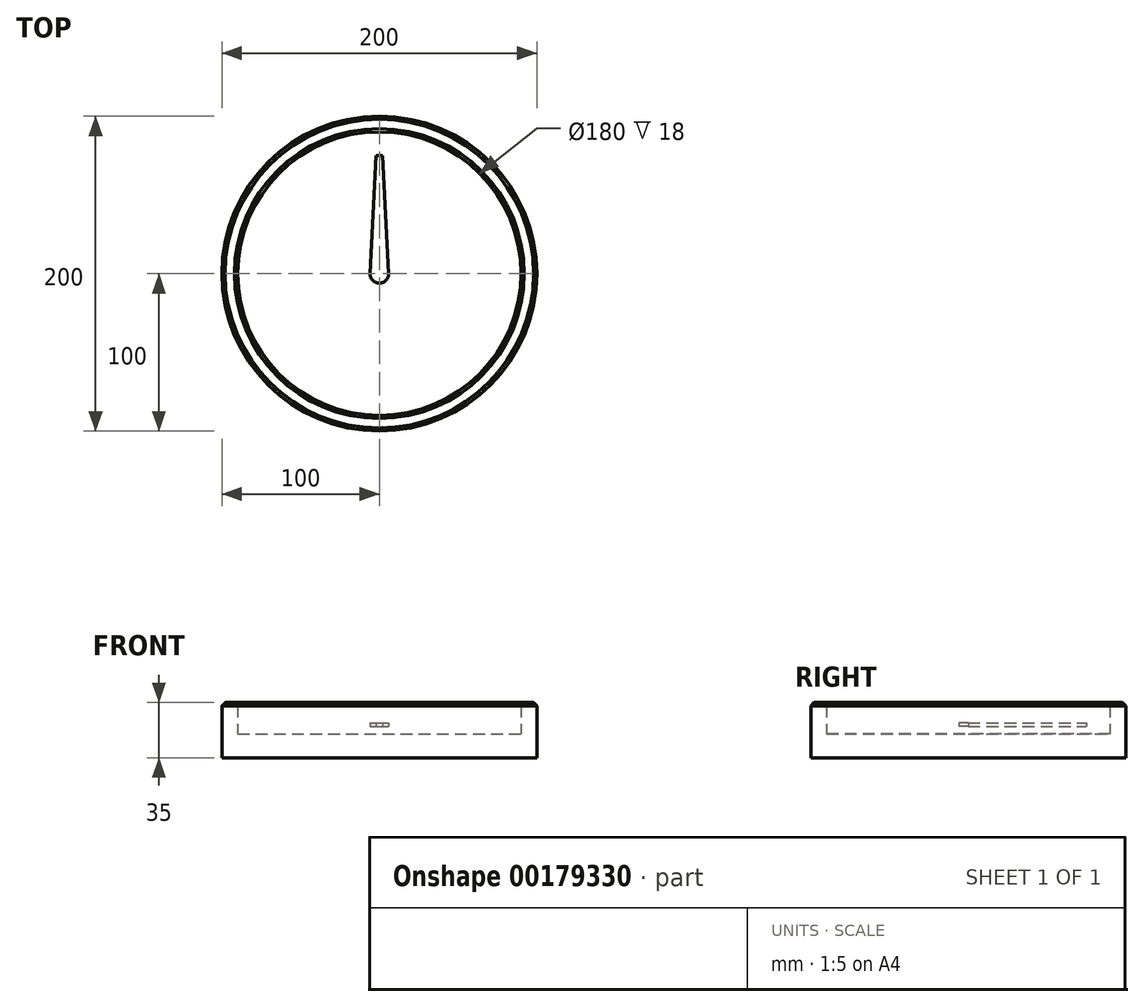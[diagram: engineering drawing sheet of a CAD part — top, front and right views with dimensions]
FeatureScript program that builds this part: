
annotation { "Feature Type Name" : "Feature", "Feature Type Description" : "" }
export const myFeature = defineFeature(function(context is Context, id is Id, definition is map)
    precondition{}
    {
        {
            var Q0;
            Q0=qCreatedBy(makeId("Front.planeOp"),FACE);
            var sketch = newSketch(context, id + "F0", { "sketchPlane" : qUnion([Q0])});
            skLineSegment(sketch, "E0.bottom", {"start": v(0, 0) * mm, "end": v(-90, 0) * mm});
            skLineSegment(sketch, "E0.top", {"start": v(0, 15) * mm, "end": v(-90, 15) * mm});
            skLineSegment(sketch, "E0.left", {"start": v(0, 0) * mm, "end": v(0, 15) * mm});
            skLineSegment(sketch, "E0.right", {"start": v(-90, 0) * mm, "end": v(-90, 15) * mm});
            skLineSegment(sketch, "E1", {"start": v(-90, 15) * mm, "end": v(-90, 35) * mm});
            skLineSegment(sketch, "E2", {"start": v(-90, 35) * mm, "end": v(-100, 35) * mm});
            skLineSegment(sketch, "E3", {"start": v(-100, 35) * mm, "end": v(-100, 0) * mm});
            skLineSegment(sketch, "E4", {"start": v(-100, 0) * mm, "end": v(-90, 0) * mm});
            skSolve(sketch);
        }
        {
            var Q0;
            Q0=makeQuery(id+"F0.imprint","IMPRINT",FACE,{"disambiguationData":[TD([[makeQuery(id+"F0.imprint","IMPRINT",EDGE,{"derivedFrom":sQuery(id+"F0.wireOp",EDGE,"E0.right")}),1.0]])]});
            var Q1;
            Q1=makeQuery(id+"F0.imprint","IMPRINT",FACE,{"disambiguationData":[TD([[makeQuery(id+"F0.imprint","IMPRINT",EDGE,{"derivedFrom":sQuery(id+"F0.wireOp",EDGE,"E0.bottom")}),-1.0]])]});
            var Q2;
            Q2=sQuery(id+"F0.wireOp",EDGE,"E0.left");
            revolve(context, id + "F1", {"entities" : qUnion([Q0, Q1]), "axis" : qUnion([Q2]), "revolveType" : RevolveType.FULL});
        }
        {
            var Q0;
            Q0=makeQuery(id+"F1.opRevolve","SWEPT_EDGE",EDGE,{"disambiguationData":[OSD([sQuery(id+"F0.wireOp",EDGE,"E2"),sQuery(id+"F0.wireOp",EDGE,"E3")])]});
            var Q1;
            Q1=makeQuery(id+"F1.opRevolve","SWEPT_EDGE",EDGE,{"disambiguationData":[OSD([sQuery(id+"F0.wireOp",EDGE,"E1"),sQuery(id+"F0.wireOp",EDGE,"E2")])]});
            chamfer(context, id + "F2", {"entities" : qUnion([Q0, Q1]), "width" : 2 * mm, "tangentPropagation" : true});
        }
        {
            var Q0;
            Q0=makeQuery(id+"F1.opRevolve","SWEPT_FACE",FACE,{"disambiguationData":[OSD([sQuery(id+"F0.wireOp",EDGE,"E0.top")])]});
            cPlane(context, id + "F3", {"entities" : qUnion([Q0]), "cplaneType" : CPlaneType.OFFSET, "offset" : 5 * mm, "width" : 150 * mm, "height" : 150 * mm});
        }
        {
            var Q0;
            Q0=qCreatedBy(id+"F3.planeOp",FACE);
            var sketch = newSketch(context, id + "F4", { "sketchPlane" : qUnion([Q0])});
            skCircle(sketch, "E5", {"center": v(0, 0) * mm, "radius": 6 * mm});
            skLineSegment(sketch, "E6", {"start": v(-6, 0) * mm, "end": v(0, 114.49) * mm});
            skLineSegment(sketch, "E7", {"start": v(0, 114.49) * mm, "end": v(0, 114.49) * mm});
            skLineSegment(sketch, "E8", {"start": v(0, 114.49) * mm, "end": v(6, 0) * mm});
            skLineSegment(sketch, "E9", {"start": v(-6, 0) * mm, "end": v(0, 0) * mm});
            skLineSegment(sketch, "E10", {"start": v(0, 0) * mm, "end": v(6, 0) * mm});
            skLineSegment(sketch, "E11", {"start": v(-2.07, 75) * mm, "end": v(2.07, 75) * mm});
            skSolve(sketch);
        }
        {
            var Q0;
            {var subQ5=sQuery(id+"F4.wireOp",EDGE,"E11");Q0=makeQuery(id+"F4.imprint","IMPRINT",FACE,{"disambiguationData":[TD([[makeQuery(id+"F4.imprint","IMPRINT",EDGE,{"derivedFrom":subQ5}),-1.0]])]});}
            var Q1;
            {var subQ0=sQuery(id+"F4.wireOp",EDGE,"E9");Q1=makeQuery(id+"F4.imprint","IMPRINT",FACE,{"disambiguationData":[TD([[makeQuery(id+"F4.imprint","IMPRINT",EDGE,{"derivedFrom":subQ0}),1.0]])]});}
            var Q2;
            {var subQ0=sQuery(id+"F4.wireOp",EDGE,"E9");Q2=makeQuery(id+"F4.imprint","IMPRINT",FACE,{"disambiguationData":[TD([[makeQuery(id+"F4.imprint","IMPRINT",EDGE,{"derivedFrom":subQ0}),-1.0]])]});}
            extrude(context, id + "F5", {"entities" : qUnion([Q0, Q1, Q2]), "depth" : 2 * mm});
        }
    });
